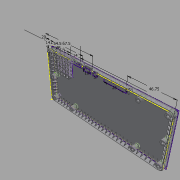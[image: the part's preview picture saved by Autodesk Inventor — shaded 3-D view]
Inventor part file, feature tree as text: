
AUTODESK INVENTOR PART (.ipt)
format: ipt  version: 2019 (Build 230136000, 136)  size: 1,154,048 bytes
history: native  units: mm
features: extrude x11, sketch x8, fillet x7, chamfer x3, hole x1
ambient origin geometry x8: Origin, YZ Plane, XZ Plane, XY Plane, X Axis, Y Axis, Z Axis, Center Point
bodies: Solid1 (feature_tree)
feature tree (30):
  sketch  "Sketch1"  dims[d0=154.0mm d1=68.0mm]
  extrude  "Extrusion1"  Depth=68.0mm
  extrude  "Extrusion2"  Depth=1.0mm
  extrude  "Extrusion3"  Depth=6.4mm TaperAngle=0.0deg
  fillet  "Fillet2"  Radius=1.3mm
  fillet  "Fillet3"  Radius=1.0mm
  fillet  "Fillet9"  Radius=0.35mm
  fillet  "Fillet4"  Radius=29.0mm
  extrude  "Extrusion10"  Depth=29.0mm
  extrude  "Extrusion11"  Depth=29.0mm
  fillet  "Fillet5"  Radius=29.0mm
  sketch  "Sketch4"  dims[d4=1.0mm d31=6.4mm d32=0.0mm d33=1.3mm d34=0.0mm d40=1.0mm d41=0.0mm d42=0.35mm d43=29.0mm]
  extrude  "Extrusion8"  Depth=29.0mm
  hole  "Hole1"  [1 undecoded]
  fillet  "Fillet6"  Radius=5.0mm
  chamfer  "Chamfer2"  Distance=0.5mm
  chamfer  "Chamfer3"  Distance=4.0mm
  sketch  "Sketch12"  dims[d49=86.0mm d50=29.0mm]
  extrude  "Extrusion12"  Depth=5.0mm
  extrude  "Extrusion13"  Depth=1.75mm
  fillet  "Fillet10"  Radius=0.25mm
  sketch  "Sketch14"  dims[d51=29.0mm d52=5.0mm d53=5.0mm]
  extrude  "Extrusion15"  Depth=1.0mm
  extrude  "Extrusion17"  Depth=2.75mm
  chamfer  "Chamfer5"  Distance=5.5mm
  extrude  "Extrusion18"  Depth=2.75mm
  sketch  "Sketch2"  dims[d2=1.0mm d3=1.0mm]
  sketch  "Sketch10"  dims[d44=86.0mm d45=29.0mm]
  sketch  "Sketch11"  dims[d46=29.0mm d47=29.0mm d48=29.0mm]
  sketch  "Sketch16"  dims[d54=2.9mm d55=6.0mm d56=5.0mm d57=3.0mm d58=90.0deg d59=8.0mm d60=20.594885mm d62=0.5mm d63=4.0mm d64=5.0mm d65=1.75mm d66=0.25mm d123=1.0mm d124=5.5mm d125=5.5mm d126=5.5mm d127=5.5mm d128=5.5mm d129=5.5mm d130=5.5mm d131=5.5mm d132=5.5mm d133=5.5mm d134=7.75mm d135=0.0mm d136=4.65mm d144=0.5mm d145=5.0mm d146=4.75mm d147=0.5mm d148=5.0mm d149=300.0mm d151=4.965mm d152=10.0mm d154=10.0mm d156=5.0mm d157=0.0mm d158=4.0mm d159=2.0mm d160=45.0deg d161=5.0mm d162=0.5mm d163=4.75mm d164=5.0mm d165=0.5mm d166=130.0mm d168=4.835mm d169=10.0mm d171=10.0mm d173=5.0mm d174=0.0mm d175=4.0mm d176=2.0mm d177=45.0deg d178=37.0mm d179=14.0mm d180=2.0mm d181=0.0mm d182=10.0mm d183=4.1mm d184=3.5mm d185=54.5mm d186=5.0mm d187=4.0mm d188=67.5mm d189=3.5mm d190=0.0mm d194=0.75mm d195=26.0mm d196=4.0mm d197=46.75mm d200=0.25mm d218=0.8mm d219=23.3mm d220=60.0mm d222=4.5mm d223=10.0mm d225=10.0mm d227=0.8mm d228=60.0mm d230=4.5mm d231=10.0mm d233=10.0mm d237=11.65mm d238=11.65mm d239=20.0mm d240=14.0mm d241=5.55mm d242=0.0mm d249=9.0mm d250=9.0mm d251=7.15mm d252=7.15mm d253=0.5mm d254=0.0mm d255=0.5mm d256=1.0mm d257=45.0deg d276=2.75mm d277=0.0mm]
note: 1 required parameter value undecoded (feature->parameter linkage not recoverable at this tier; creation-order binding heuristic only, values carry confidence <= 0.55)
